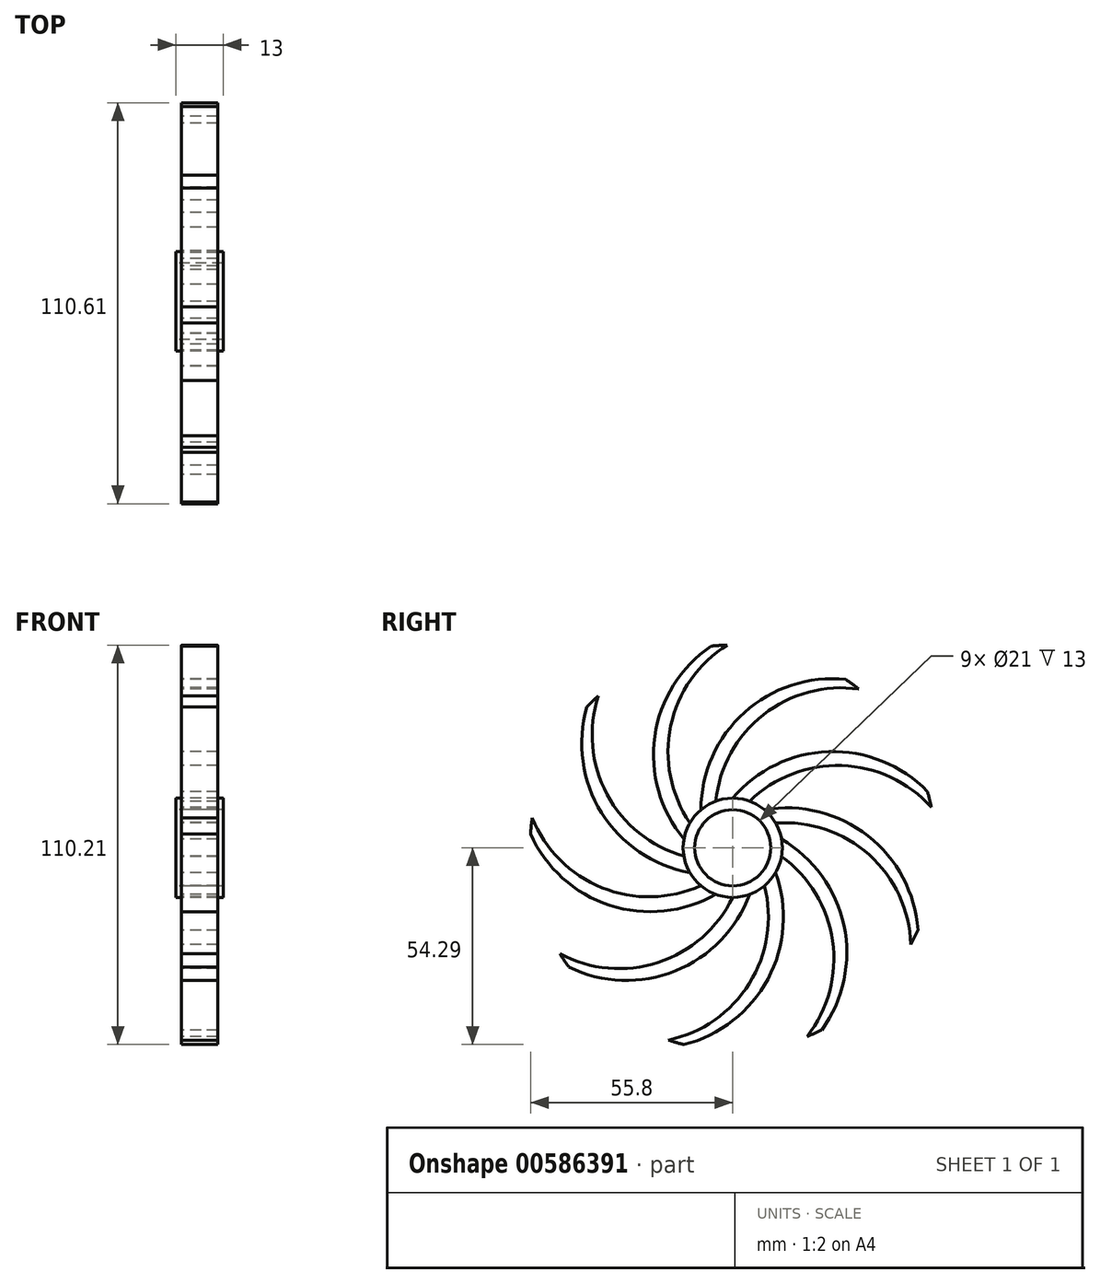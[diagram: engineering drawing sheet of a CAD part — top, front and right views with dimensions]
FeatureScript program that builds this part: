
annotation { "Feature Type Name" : "Feature", "Feature Type Description" : "" }
export const myFeature = defineFeature(function(context is Context, id is Id, definition is map)
    precondition{}
    {
        {
            var Q0;
            Q0=qCreatedBy(makeId("Right.planeOp"),FACE);
            var sketch = newSketch(context, id + "F0", { "sketchPlane" : qUnion([Q0])});
            skCircle(sketch, "E0", {"center": v(0, 0) * mm, "radius": 10.5 * mm});
            skCircle(sketch, "E1", {"center": v(0, 0) * mm, "radius": 13.68 * mm});
            skArc(sketch, "E2", {"start": v(53.75, 15.5) * mm, "mid": v(26.47, 26.51) * mm, "end": v(0, 13.68) * mm});
            skCircle(sketch, "E3", {"center": v(0, 0) * mm, "radius": 55.94 * mm});
            skArc(sketch, "E4", {"start": v(54.8, 11.17) * mm, "mid": v(30.11, 22.68) * mm, "end": v(4.7, 12.84) * mm});
            skCircle(sketch, "E5", {"center": v(0, 0) * mm, "radius": 59.61 * mm});
            skSolve(sketch);
        }
        {
            var Q0;
            Q0=makeQuery(id+"F0.imprint","IMPRINT",FACE,{"disambiguationData":[TD([[makeQuery(id+"F0.imprint","IMPRINT",EDGE,{"derivedFrom":sQuery(id+"F0.wireOp",EDGE,"E0")}),-1.0]])]});
            extrude(context, id + "F1", {"entities" : qUnion([Q0]), "depth" : 6.5 * mm, "offsetDistance" : 25.4 * mm, "hasSecondDirection" : true, "secondDirectionOppositeDirection" : true, "secondDirectionDepth" : 6.5 * mm});
        }
        {
            var Q0;
            {var subQ0=sQuery(id+"F0.wireOp",EDGE,"E2");Q0=makeQuery(id+"F0.imprint","IMPRINT",FACE,{"disambiguationData":[TD([[makeQuery(id+"F0.imprint","IMPRINT",EDGE,{"derivedFrom":subQ0}),1.0]])]});}
            extrude(context, id + "F2", {"entities" : qUnion([Q0]), "operationType" : NewBodyOperationType.ADD, "depth" : 5 * mm, "offsetDistance" : 25.4 * mm, "hasSecondDirection" : true, "secondDirectionOppositeDirection" : true, "secondDirectionDepth" : 5 * mm});
        }
        {
            var Q0;
            Q0=makeQuery(id+"F1.opExtrude","SWEPT_BODY",BODY,{"disambiguationData":[OSD([sQuery(id+"F0.wireOp",EDGE,"E0"),sQuery(id+"F0.wireOp",EDGE,"E1")])]});
            var Q1;
            Q1=makeQuery(id+"F1.opExtrude","CAP_EDGE",EDGE,{"disambiguationData":[OSD([sQuery(id+"F0.wireOp",EDGE,"E1")])],"isStart":false});
            circularPattern(context, id + "F3", {"entities" : qUnion([Q0]), "axis" : qUnion([Q1]), "angle" : 360 * degree, "instanceCount" : 9, "equalSpace" : true});
        }
    });
